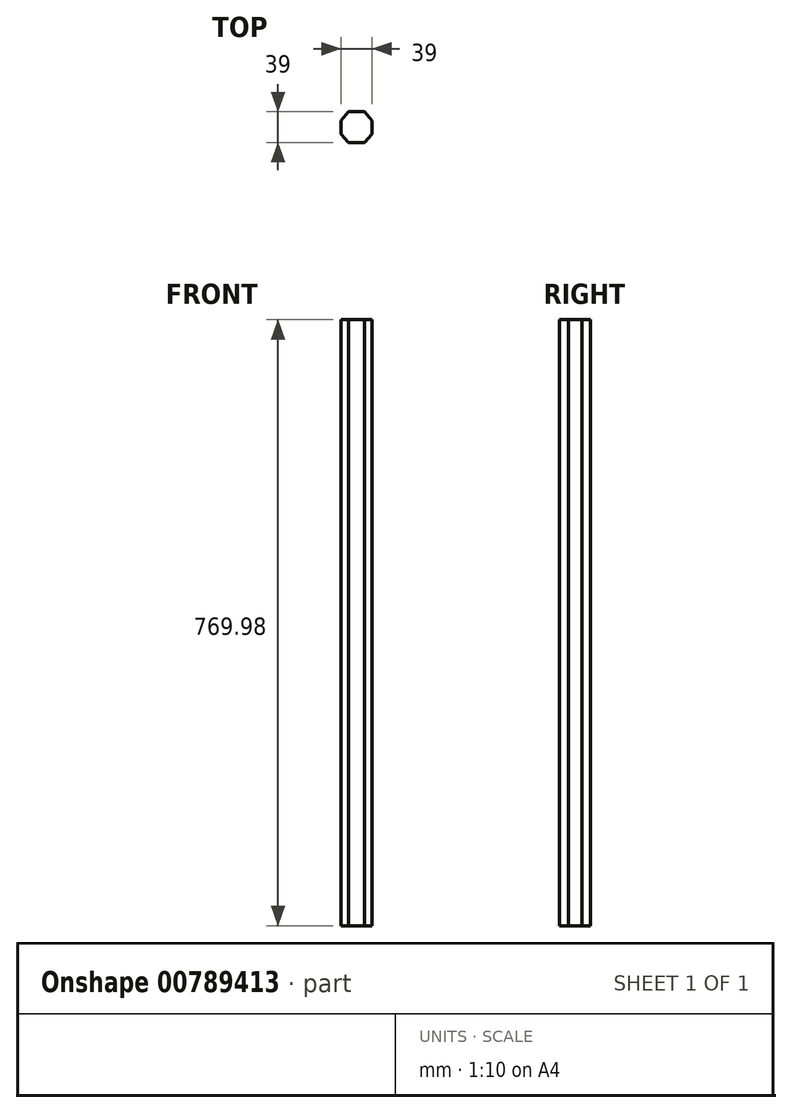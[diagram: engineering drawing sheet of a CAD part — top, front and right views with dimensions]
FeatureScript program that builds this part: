
annotation { "Feature Type Name" : "Feature", "Feature Type Description" : "" }
export const myFeature = defineFeature(function(context is Context, id is Id, definition is map)
    precondition{}
    {
        {
            var Q0;
            Q0=qCreatedBy(makeId("Top.planeOp"),FACE);
            var sketch = newSketch(context, id + "F0", { "sketchPlane" : qUnion([Q0])});
            skLineSegment(sketch, "E0", {"start": v(-39, 0) * mm, "end": v(-39, -17.1) * mm});
            skLineSegment(sketch, "E1", {"start": v(-39, -17.1) * mm, "end": v(-29.9, -28.05) * mm});
            skLineSegment(sketch, "E2", {"start": v(-29.9, -28.05) * mm, "end": v(-9.1, -28.05) * mm});
            skLineSegment(sketch, "E3", {"start": v(-9.1, -28.05) * mm, "end": v(0, -17.1) * mm});
            skLineSegment(sketch, "E4", {"start": v(0, -17.1) * mm, "end": v(0, 0) * mm});
            skLineSegment(sketch, "E5", {"start": v(0, 0) * mm, "end": v(-9.1, 10.95) * mm});
            skLineSegment(sketch, "E6", {"start": v(-9.1, 10.95) * mm, "end": v(-29.9, 10.95) * mm});
            skLineSegment(sketch, "E7", {"start": v(-29.9, 10.95) * mm, "end": v(-39, 0) * mm});
            skPoint(sketch, "E8", {"position": v(-19.5, -28.05) * mm});
            skPoint(sketch, "E9", {"position": v(-34.45, -22.58) * mm});
            skPoint(sketch, "E10", {"position": v(-39, -8.55) * mm});
            skPoint(sketch, "E11", {"position": v(-34.45, 5.47) * mm});
            skPoint(sketch, "E12", {"position": v(-19.5, 10.95) * mm});
            skPoint(sketch, "E13", {"position": v(-4.55, 5.47) * mm});
            skPoint(sketch, "E14", {"position": v(0, -8.55) * mm});
            skPoint(sketch, "E15", {"position": v(-4.55, -22.58) * mm});
            skLineSegment(sketch, "E16", {"start": v(12.16, 40.88) * mm, "end": v(12.16, 24.78) * mm});
            skLineSegment(sketch, "E17", {"start": v(12.16, 24.78) * mm, "end": v(20.4, 14.83) * mm});
            skLineSegment(sketch, "E18", {"start": v(39.93, 14.83) * mm, "end": v(48.16, 24.78) * mm});
            skLineSegment(sketch, "E19", {"start": v(48.16, 24.78) * mm, "end": v(48.16, 40.88) * mm});
            skLineSegment(sketch, "E20", {"start": v(48.16, 40.88) * mm, "end": v(39.93, 50.83) * mm});
            skLineSegment(sketch, "E21", {"start": v(39.93, 50.83) * mm, "end": v(20.4, 50.83) * mm});
            skLineSegment(sketch, "E22", {"start": v(20.4, 50.83) * mm, "end": v(12.16, 40.88) * mm});
            skPoint(sketch, "E23", {"position": v(30.16, 14.83) * mm});
            skPoint(sketch, "E24", {"position": v(16.28, 19.8) * mm});
            skPoint(sketch, "E25", {"position": v(12.16, 32.83) * mm});
            skPoint(sketch, "E26", {"position": v(16.28, 45.86) * mm});
            skPoint(sketch, "E27", {"position": v(30.16, 50.83) * mm});
            skPoint(sketch, "E28", {"position": v(44.04, 45.86) * mm});
            skPoint(sketch, "E29", {"position": v(48.16, 32.83) * mm});
            skPoint(sketch, "E30", {"position": v(44.04, 19.8) * mm});
            skLineSegment(sketch, "E31", {"start": v(20.4, 14.83) * mm, "end": v(25.28, 14.83) * mm});
            skLineSegment(sketch, "E32", {"start": v(39.93, 14.83) * mm, "end": v(35.04, 14.83) * mm});
            skSolve(sketch);
        }
        {
            var Q0;
            Q0=makeQuery(id+"F0.imprint","IMPRINT",FACE,{"disambiguationData":[TD([[makeQuery(id+"F0.imprint","IMPRINT",EDGE,{"derivedFrom":sQuery(id+"F0.wireOp",EDGE,"E0")}),1.0]])]});
            extrude(context, id + "F1", {"entities" : qUnion([Q0]), "depth" : 762 * mm, "offsetDistance" : 25 * mm});
        }
        {
            var Q0;
            Q0=makeQuery(id+"F1.opExtrude","CAP_FACE",FACE,{"disambiguationData":[OSD([sQuery(id+"F0.wireOp",EDGE,"E0"),sQuery(id+"F0.wireOp",EDGE,"E1"),sQuery(id+"F0.wireOp",EDGE,"E2"),sQuery(id+"F0.wireOp",EDGE,"E3"),sQuery(id+"F0.wireOp",EDGE,"E4"),sQuery(id+"F0.wireOp",EDGE,"E5"),sQuery(id+"F0.wireOp",EDGE,"E6"),sQuery(id+"F0.wireOp",EDGE,"E7")])],"isStart":false});
            var Q1;
            Q1=makeQuery(id+"F1.opExtrude","CAP_FACE",FACE,{"disambiguationData":[OSD([sQuery(id+"F0.wireOp",EDGE,"E16"),sQuery(id+"F0.wireOp",EDGE,"E17"),sQuery(id+"F0.wireOp",EDGE,"1c81f20d-029b-4431-8c03-4020a2a8b489"),sQuery(id+"F0.wireOp",EDGE,"E18"),sQuery(id+"F0.wireOp",EDGE,"E19"),sQuery(id+"F0.wireOp",EDGE,"E20"),sQuery(id+"F0.wireOp",EDGE,"E21"),sQuery(id+"F0.wireOp",EDGE,"E22")])],"isStart":false});
            var Q2;
            Q2=makeQuery(id+"F1.opExtrude","CAP_FACE",FACE,{"disambiguationData":[OSD([sQuery(id+"F0.wireOp",EDGE,"E0"),sQuery(id+"F0.wireOp",EDGE,"E1"),sQuery(id+"F0.wireOp",EDGE,"E2"),sQuery(id+"F0.wireOp",EDGE,"E3"),sQuery(id+"F0.wireOp",EDGE,"E4"),sQuery(id+"F0.wireOp",EDGE,"E5"),sQuery(id+"F0.wireOp",EDGE,"E6"),sQuery(id+"F0.wireOp",EDGE,"E7")])],"isStart":true});
            var Q3;
            Q3=makeQuery(id+"F1.opExtrude","CAP_FACE",FACE,{"disambiguationData":[OSD([sQuery(id+"F0.wireOp",EDGE,"E16"),sQuery(id+"F0.wireOp",EDGE,"E17"),sQuery(id+"F0.wireOp",EDGE,"1c81f20d-029b-4431-8c03-4020a2a8b489"),sQuery(id+"F0.wireOp",EDGE,"E18"),sQuery(id+"F0.wireOp",EDGE,"E19"),sQuery(id+"F0.wireOp",EDGE,"E20"),sQuery(id+"F0.wireOp",EDGE,"E21"),sQuery(id+"F0.wireOp",EDGE,"E22")])],"isStart":true});
            shell(context, id + "F2", {"entities" : qUnion([Q0, Q1, Q2, Q3]), "thickness" : 2.5 * mm});
        }
        {
            var Q0;
            Q0=qSketchRegion(id+"F0",true);
            extrude(context, id + "F3", {"entities" : qUnion([Q0]), "operationType" : NewBodyOperationType.ADD, "endBound" : BoundingType.THROUGH_ALL, "depth" : 25 * mm, "offsetDistance" : 25 * mm});
        }
    });
